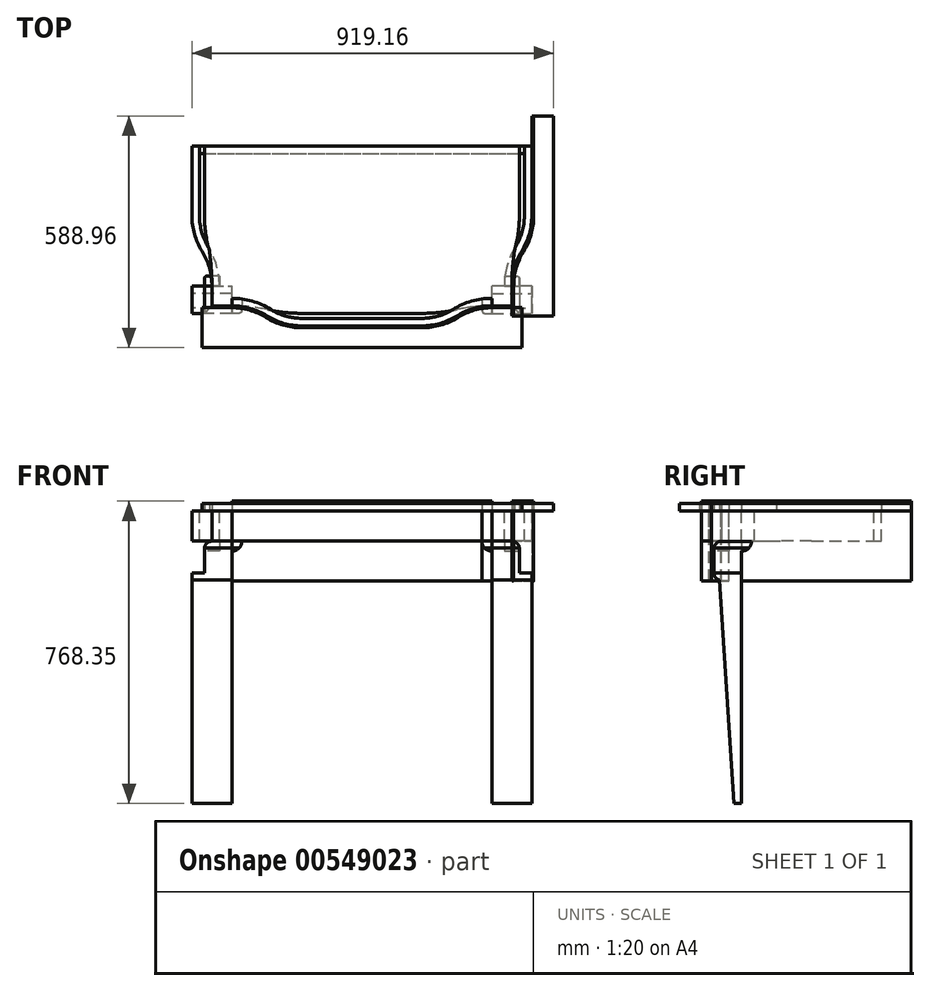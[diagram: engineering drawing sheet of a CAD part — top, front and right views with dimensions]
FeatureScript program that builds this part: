
annotation { "Feature Type Name" : "Feature", "Feature Type Description" : "" }
export const myFeature = defineFeature(function(context is Context, id is Id, definition is map)
    precondition{}
    {
        {
            var Q0;
            Q0=qCreatedBy(makeId("Top.planeOp"),FACE);
            var sketch = newSketch(context, id + "F0", { "sketchPlane" : qUnion([Q0])});
            skLineSegment(sketch, "E0.bottom", {"start": v(381, -203.2) * mm, "end": v(-381, -203.2) * mm});
            skLineSegment(sketch, "E0.top", {"start": v(381, 203.2) * mm, "end": v(-381, 203.2) * mm});
            skLineSegment(sketch, "E0.left", {"start": v(381, -203.2) * mm, "end": v(381, 203.2) * mm});
            skLineSegment(sketch, "E0.right", {"start": v(-381, -203.2) * mm, "end": v(-381, 203.2) * mm});
            skPoint(sketch, "E0.middle", {"position": v(0, 0) * mm});
            skSolve(sketch);
        }
        {
            var Q0;
            Q0=makeQuery(id+"F0.imprint","IMPRINT",FACE,{"disambiguationData":[TD([[makeQuery(id+"F0.imprint","IMPRINT",EDGE,{"derivedFrom":sQuery(id+"F0.wireOp",EDGE,"E0.bottom")}),-1.0]])]});
            var sketch = newSketch(context, id + "F1", { "sketchPlane" : qUnion([Q0])});
            skLineSegment(sketch, "E1.0", {"start": v(-330.2, -203.2) * mm, "end": v(-381, -203.2) * mm});
            skLineSegment(sketch, "E2.right", {"start": v(330.2, -203.2) * mm, "end": v(330.2, -184.15) * mm});
            skLineSegment(sketch, "E3", {"start": v(0, -254) * mm, "end": v(0, 0) * mm, "construction": true});
            skArc(sketch, "E4", {"start": v(-330.2, -203.2) * mm, "mid": v(-283.97, -209.67) * mm, "end": v(-241.3, -228.6) * mm});
            skArc(sketch, "E5", {"start": v(-241.3, -228.6) * mm, "mid": v(-198.63, -247.53) * mm, "end": v(-152.4, -254) * mm});
            skLineSegment(sketch, "E6", {"start": v(-152.4, -254) * mm, "end": v(0, -254) * mm});
            skArc(sketch, "E7.MirrorCS", {"start": v(330.2, -203.2) * mm, "mid": v(283.97, -209.67) * mm, "end": v(241.3, -228.6) * mm});
            skArc(sketch, "E8.MirrorCS", {"start": v(241.3, -228.6) * mm, "mid": v(198.63, -247.53) * mm, "end": v(152.4, -254) * mm});
            skPoint(sketch, "E9.orphan", {"position": v(-381, -254) * mm});
            skPoint(sketch, "E10.orphan", {"position": v(381, -254) * mm});
            skLineSegment(sketch, "E11.MirrorCS", {"start": v(152.4, -254) * mm, "end": v(0, -254) * mm});
            skArc(sketch, "E12.0", {"start": v(-231.24, -212.43) * mm, "mid": v(-193.4, -229.2) * mm, "end": v(-152.4, -234.95) * mm});
            skArc(sketch, "E12.1", {"start": v(-330.2, -184.15) * mm, "mid": v(-278.74, -191.36) * mm, "end": v(-231.24, -212.43) * mm});
            skArc(sketch, "E13.0", {"start": v(231.24, -212.43) * mm, "mid": v(193.4, -229.2) * mm, "end": v(152.4, -234.95) * mm});
            skArc(sketch, "E13.1", {"start": v(330.2, -184.15) * mm, "mid": v(278.74, -191.36) * mm, "end": v(231.24, -212.43) * mm});
            skPoint(sketch, "E14.0.end.orphan", {"position": v(381, 203.2) * mm});
            skPoint(sketch, "E14.0.start.orphan", {"position": v(381, -203.2) * mm});
            skPoint(sketch, "E15.0.end.orphan", {"position": v(-381, 203.2) * mm});
            skPoint(sketch, "E15.0.start.orphan", {"position": v(-381, -203.2) * mm});
            skLineSegment(sketch, "E16", {"start": v(-152.4, -234.95) * mm, "end": v(152.4, -234.95) * mm});
            skLineSegment(sketch, "E17", {"start": v(-330.2, -184.15) * mm, "end": v(-330.2, -203.2) * mm});
            skSolve(sketch);
        }
        {
            var Q0;
            Q0=makeQuery(id+"F0.imprint","IMPRINT",FACE,{"disambiguationData":[TD([[makeQuery(id+"F0.imprint","IMPRINT",EDGE,{"derivedFrom":sQuery(id+"F0.wireOp",EDGE,"E0.bottom")}),-1.0]])]});
            var sketch = newSketch(context, id + "F2", { "sketchPlane" : qUnion([Q0])});
            skLineSegment(sketch, "E18.0", {"start": v(381, -203.2) * mm, "end": v(-381, -203.2) * mm, "construction": true});
            skLineSegment(sketch, "E19.0", {"start": v(-381, -203.2) * mm, "end": v(-381, 203.2) * mm, "construction": true});
            skLineSegment(sketch, "E20.0", {"start": v(381, -203.2) * mm, "end": v(381, 203.2) * mm, "construction": true});
            skLineSegment(sketch, "E21.bottom", {"start": v(431.8, -254) * mm, "end": v(330.2, -254) * mm});
            skLineSegment(sketch, "E21.top", {"start": v(431.8, -152.4) * mm, "end": v(330.2, -152.4) * mm});
            skLineSegment(sketch, "E21.left", {"start": v(431.8, -254) * mm, "end": v(431.8, -152.4) * mm});
            skLineSegment(sketch, "E21.right", {"start": v(330.2, -254) * mm, "end": v(330.2, -152.4) * mm});
            skPoint(sketch, "E21.middle", {"position": v(381, -203.2) * mm});
            skPoint(sketch, "E22.middle", {"position": v(-381, -203.2) * mm});
            skSolve(sketch);
        }
        {
            var Q0;
            Q0=makeQuery(id+"F0.imprint","IMPRINT",FACE,{"disambiguationData":[TD([[makeQuery(id+"F0.imprint","IMPRINT",EDGE,{"derivedFrom":sQuery(id+"F0.wireOp",EDGE,"E0.bottom")}),-1.0]])]});
            var sketch = newSketch(context, id + "F3", { "sketchPlane" : qUnion([Q0])});
            skLineSegment(sketch, "E23.0", {"start": v(-381, -203.2) * mm, "end": v(-381, 203.2) * mm, "construction": true});
            skLineSegment(sketch, "E24.0", {"start": v(-361.95, -152.4) * mm, "end": v(-381, -152.4) * mm});
            skArc(sketch, "E25", {"start": v(-381, -152.4) * mm, "mid": v(-387.47, -106.17) * mm, "end": v(-406.4, -63.5) * mm});
            skArc(sketch, "E26", {"start": v(-431.8, 25.4) * mm, "mid": v(-425.33, -20.83) * mm, "end": v(-406.4, -63.5) * mm});
            skLineSegment(sketch, "E27", {"start": v(-431.8, 25.4) * mm, "end": v(-431.8, 203.2) * mm});
            skArc(sketch, "E28.0", {"start": v(-412.75, 25.4) * mm, "mid": v(-407, -15.6) * mm, "end": v(-390.23, -53.44) * mm});
            skArc(sketch, "E28.1", {"start": v(-361.95, -152.4) * mm, "mid": v(-369.16, -100.94) * mm, "end": v(-390.23, -53.44) * mm});
            skLineSegment(sketch, "E29", {"start": v(-412.75, 25.4) * mm, "end": v(-412.75, 203.2) * mm});
            skLineSegment(sketch, "E30", {"start": v(-412.75, 203.2) * mm, "end": v(-431.8, 203.2) * mm});
            skPoint(sketch, "E31.orphan", {"position": v(-330.2, -152.4) * mm});
            skSolve(sketch);
        }
        {
            var Q0;
            Q0 = qSketchRegion(id + "F3", true);
            extrude(context, id + "F4", {"entities" : qUnion([Q0]), "oppositeDirection" : true, "depth" : 76.2 * mm, "offsetDistance" : 25.4 * mm});
        }
        {
            var Q0;
            Q0 = qSketchRegion(id + "F1", true);
            extrude(context, id + "F5", {"entities" : qUnion([Q0]), "oppositeDirection" : true, "depth" : 76.2 * mm, "offsetDistance" : 25.4 * mm});
        }
        {
            var Q0;
            Q0=makeQuery(id+"F4.opExtrude","SWEPT_BODY",BODY,{"disambiguationData":[OSD([sQuery(id+"F3.wireOp",EDGE,"E24.0"),sQuery(id+"F3.wireOp",EDGE,"E25"),sQuery(id+"F3.wireOp",EDGE,"E26"),sQuery(id+"F3.wireOp",EDGE,"E27"),sQuery(id+"F3.wireOp",EDGE,"E28.0"),sQuery(id+"F3.wireOp",EDGE,"E28.1"),sQuery(id+"F3.wireOp",EDGE,"E29"),sQuery(id+"F3.wireOp",EDGE,"E30")])]});
            var Q1;
            Q1=qCreatedBy(makeId("Right.planeOp"),FACE);
            mirror(context, id + "F6", {"entities" : qUnion([Q0]), "mirrorPlane" : qUnion([Q1])});
        }
        {
            var Q0;
            Q0=makeQuery(id+"F0.imprint","IMPRINT",FACE,{"disambiguationData":[TD([[makeQuery(id+"F0.imprint","IMPRINT",EDGE,{"derivedFrom":sQuery(id+"F0.wireOp",EDGE,"E0.bottom")}),-1.0]])]});
            var sketch = newSketch(context, id + "F7", { "sketchPlane" : qUnion([Q0])});
            skLineSegment(sketch, "E32.0", {"start": v(-381, -203.2) * mm, "end": v(-381, 203.2) * mm, "construction": true});
            skArc(sketch, "E33", {"start": v(-381, -152.4) * mm, "mid": v(-382.59, -107.84) * mm, "end": v(-387.35, -63.5) * mm});
            skLineSegment(sketch, "E34.0", {"start": v(-400.05, 25.4) * mm, "end": v(-400.05, 203.2) * mm});
            skArc(sketch, "E35", {"start": v(-400.05, 25.4) * mm, "mid": v(-396.86, -19.5) * mm, "end": v(-387.35, -63.5) * mm});
            skLineSegment(sketch, "E36", {"start": v(-381, -152.4) * mm, "end": v(-381, -203.2) * mm});
            skPoint(sketch, "E37.0.start.orphan", {"position": v(-330.2, -152.4) * mm});
            skLineSegment(sketch, "E38.0", {"start": v(-152.4, -222.25) * mm, "end": v(152.4, -222.25) * mm});
            skPoint(sketch, "E39.0.end.orphan", {"position": v(-381, -203.2) * mm});
            skPoint(sketch, "E39.0.start.orphan", {"position": v(381, -203.2) * mm});
            skLineSegment(sketch, "E40.0", {"start": v(-330.2, -203.2) * mm, "end": v(-330.2, -152.4) * mm, "construction": true});
            skArc(sketch, "E41", {"start": v(-241.3, -212.73) * mm, "mid": v(-285.5, -205.59) * mm, "end": v(-330.2, -203.2) * mm});
            skArc(sketch, "E42", {"start": v(-241.3, -212.73) * mm, "mid": v(-197.1, -219.86) * mm, "end": v(-152.4, -222.25) * mm});
            skLineSegment(sketch, "E43", {"start": v(-381, -203.2) * mm, "end": v(-330.2, -203.2) * mm});
            skArc(sketch, "E44.MirrorCS", {"start": v(241.3, -212.73) * mm, "mid": v(197.1, -219.86) * mm, "end": v(152.4, -222.25) * mm});
            skArc(sketch, "E45.MirrorCS", {"start": v(241.3, -212.73) * mm, "mid": v(285.5, -205.59) * mm, "end": v(330.2, -203.2) * mm});
            skArc(sketch, "E46.MirrorCS", {"start": v(381, -152.4) * mm, "mid": v(382.59, -107.84) * mm, "end": v(387.35, -63.5) * mm});
            skArc(sketch, "E47.MirrorCS", {"start": v(400.05, 25.4) * mm, "mid": v(396.86, -19.5) * mm, "end": v(387.35, -63.5) * mm});
            skLineSegment(sketch, "E48.MirrorCS", {"start": v(400.05, 25.4) * mm, "end": v(400.05, 203.2) * mm});
            skLineSegment(sketch, "E49.MirrorCS", {"start": v(381, -203.2) * mm, "end": v(330.2, -203.2) * mm});
            skLineSegment(sketch, "E50", {"start": v(381, -152.4) * mm, "end": v(381, -203.2) * mm});
            skLineSegment(sketch, "E51", {"start": v(-400.05, 203.2) * mm, "end": v(400.05, 203.2) * mm});
            skSolve(sketch);
        }
        {
            var Q0;
            Q0 = qSketchRegion(id + "F7", true);
            extrude(context, id + "F8", {"entities" : qUnion([Q0]), "depth" : 19.05 * mm, "offsetDistance" : 25.4 * mm});
        }
        {
            var Q0;
            Q0 = qSketchRegion(id + "F2", true);
            extrude(context, id + "F9", {"entities" : qUnion([Q0]), "oppositeDirection" : true, "depth" : 742.95 * mm, "offsetDistance" : 25.4 * mm});
        }
        {
            var Q0;
            Q0=makeQuery(id+"F9.opExtrude","SWEPT_FACE",FACE,{"disambiguationData":[OSD([sQuery(id+"F2.wireOp",EDGE,"E21.left")])]});
            var sketch = newSketch(context, id + "F10", { "sketchPlane" : qUnion([Q0])});
            skLineSegment(sketch, "E52", {"start": v(-203.2, -76.2) * mm, "end": v(-152.4, -76.2) * mm, "construction": true});
            skLineSegment(sketch, "E53", {"start": v(-203.2, 0) * mm, "end": v(-203.2, -76.2) * mm});
            skArc(sketch, "E54", {"start": v(-203.2, -76.2) * mm, "mid": v(-216.03, -81.17) * mm, "end": v(-222.17, -93.49) * mm});
            skLineSegment(sketch, "E55", {"start": v(-222.17, -93.49) * mm, "end": v(-222.17, -156.99) * mm});
            skPoint(sketch, "E56.end.orphan", {"position": v(-171.45, -742.95) * mm});
            skArc(sketch, "E57", {"start": v(-222.17, -156.99) * mm, "mid": v(-218.46, -168.28) * mm, "end": v(-208.78, -175.18) * mm});
            skLineSegment(sketch, "E58", {"start": v(-208.78, -175.18) * mm, "end": v(-171.45, -742.95) * mm});
            skSolve(sketch);
        }
        {
            var Q0;
            {var subQ0=sQuery(id+"F10.wireOp",EDGE,"E53");Q0=makeQuery(id+"F10.imprint","IMPRINT",FACE,{"disambiguationData":[TD([[makeQuery(id+"F10.imprint","IMPRINT",EDGE,{"derivedFrom":subQ0}),-1.0]])]});}
            extrude(context, id + "F11", {"entities" : qUnion([Q0]), "operationType" : NewBodyOperationType.REMOVE, "oppositeDirection" : true, "depth" : 127 * mm, "offsetDistance" : 25.4 * mm});
        }
        {
            var Q0;
            Q0=makeQuery(id+"F11.boolean.opBoolean","COPY",FACE,{"derivedFrom":makeQuery(id+"F11.opExtrude","SWEPT_FACE",FACE,{"disambiguationData":[OSD([sQuery(id+"F10.wireOp",EDGE,"E55")])]})});
            var sketch = newSketch(context, id + "F12", { "sketchPlane" : qUnion([Q0])});
            skLineSegment(sketch, "E59.0", {"start": v(381, 0) * mm, "end": v(431.8, 0) * mm});
            skLineSegment(sketch, "E60.0", {"start": v(431.8, 0) * mm, "end": v(431.8, -76.2) * mm});
            skLineSegment(sketch, "E61", {"start": v(381, 0) * mm, "end": v(381, -76.2) * mm});
            skArc(sketch, "E62", {"start": v(399.97, -93.55) * mm, "mid": v(393.85, -81.19) * mm, "end": v(381, -76.2) * mm});
            skLineSegment(sketch, "E63", {"start": v(399.97, -93.55) * mm, "end": v(399.97, -156.99) * mm});
            skArc(sketch, "E64", {"start": v(399.97, -156.99) * mm, "mid": v(396.42, -168.07) * mm, "end": v(387.08, -175.02) * mm});
            skLineSegment(sketch, "E65", {"start": v(387.08, -175.02) * mm, "end": v(349.25, -742.95) * mm});
            skPoint(sketch, "E66.0", {"position": v(381, -742.95) * mm});
            skLineSegment(sketch, "E67.0", {"start": v(349.25, -742.95) * mm, "end": v(431.8, -742.95) * mm});
            skLineSegment(sketch, "E68.0", {"start": v(431.8, -175.18) * mm, "end": v(431.8, -742.95) * mm});
            skPoint(sketch, "E69.orphan", {"position": v(330.2, -742.95) * mm});
            skLineSegment(sketch, "E70.0", {"start": v(431.8, -156.99) * mm, "end": v(431.8, -175.18) * mm});
            skLineSegment(sketch, "E71.0", {"start": v(431.8, -93.49) * mm, "end": v(431.8, -156.99) * mm});
            skPoint(sketch, "E72.0", {"position": v(431.8, -81.17) * mm});
            skLineSegment(sketch, "E73.0", {"start": v(431.8, -76.2) * mm, "end": v(431.8, -93.49) * mm});
            skPoint(sketch, "E74.orphan", {"position": v(330.2, 0) * mm});
            skSolve(sketch);
        }
        {
            var Q0;
            {var subQ0=sQuery(id+"F12.wireOp",EDGE,"E64");Q0=makeQuery(id+"F12.imprint","IMPRINT",FACE,{"disambiguationData":[TD([[makeQuery(id+"F12.imprint","IMPRINT",EDGE,{"derivedFrom":subQ0}),1.0]])]});}
            var Q1;
            {var subQ5=sQuery(id+"F12.wireOp",EDGE,"E63");Q1=makeQuery(id+"F12.imprint","IMPRINT",FACE,{"disambiguationData":[TD([[makeQuery(id+"F12.imprint","IMPRINT",EDGE,{"derivedFrom":subQ5}),1.0]])]});}
            var Q2;
            Q2=makeQuery(id+"F12.imprint","IMPRINT",FACE,{"disambiguationData":[TD([[makeQuery(id+"F12.imprint","IMPRINT",EDGE,{"derivedFrom":sQuery(id+"F12.wireOp",EDGE,"E59.0")}),-1.0]])]});
            extrude(context, id + "F13", {"entities" : qUnion([Q0, Q1, Q2]), "operationType" : NewBodyOperationType.REMOVE, "oppositeDirection" : true, "depth" : 101.6 * mm, "offsetDistance" : 25.4 * mm});
        }
        {
            var Q0;
            Q0=makeQuery(id+"F9.opExtrude","SWEPT_BODY",BODY,{"disambiguationData":[OSD([sQuery(id+"F2.wireOp",EDGE,"E21.bottom"),sQuery(id+"F2.wireOp",EDGE,"E21.top"),sQuery(id+"F2.wireOp",EDGE,"E21.left"),sQuery(id+"F2.wireOp",EDGE,"E21.right")])]});
            var Q1;
            Q1=qCreatedBy(makeId("Right.planeOp"),FACE);
            mirror(context, id + "F14", {"entities" : qUnion([Q0]), "mirrorPlane" : qUnion([Q1])});
        }
        {
            var Q0;
            Q0=makeQuery(id+"F9.opExtrude","SWEPT_FACE",FACE,{"disambiguationData":[OSD([sQuery(id+"F2.wireOp",EDGE,"E21.right")])]});
            var sketch = newSketch(context, id + "F15", { "sketchPlane" : qUnion([Q0])});
            skLineSegment(sketch, "E75.0", {"start": v(152.4, -742.95) * mm, "end": v(152.4, 0) * mm, "construction": true});
            skLineSegment(sketch, "E76.0.0", {"start": v(171.45, -742.95) * mm, "end": v(208.78, -175.18) * mm, "construction": true});
            skArc(sketch, "E76.0.1", {"start": v(208.78, -175.18) * mm, "mid": v(218.46, -168.28) * mm, "end": v(222.17, -156.99) * mm, "construction": true});
            skLineSegment(sketch, "E76.0.2", {"start": v(222.17, -156.99) * mm, "end": v(222.17, -93.49) * mm, "construction": true});
            skArc(sketch, "E76.0.3", {"start": v(222.17, -93.49) * mm, "mid": v(216.03, -81.17) * mm, "end": v(203.2, -76.2) * mm});
            skLineSegment(sketch, "E76.0.4", {"start": v(203.2, -76.2) * mm, "end": v(203.2, 0) * mm});
            skLineSegment(sketch, "E76.0.5", {"start": v(203.2, 0) * mm, "end": v(152.4, 0) * mm, "construction": true});
            skLineSegment(sketch, "E76.0.6", {"start": v(152.4, 0) * mm, "end": v(152.4, -742.95) * mm});
            skLineSegment(sketch, "E76.0.7", {"start": v(152.4, -742.95) * mm, "end": v(171.45, -742.95) * mm, "construction": true});
            skLineSegment(sketch, "E77.0", {"start": v(184.15, -76.2) * mm, "end": v(184.15, 0) * mm, "construction": true});
            skLineSegment(sketch, "E78.0", {"start": v(184.15, -76.2) * mm, "end": v(203.2, -76.2) * mm});
            skLineSegment(sketch, "E79", {"start": v(184.15, -76.2) * mm, "end": v(184.15, -101.6) * mm});
            skLineSegment(sketch, "E80", {"start": v(184.15, -101.6) * mm, "end": v(222.17, -101.6) * mm});
            skSolve(sketch);
        }
        {
            var Q0;
            {var subQ1=sQuery(id+"F15.wireOp",EDGE,"E76.0.3");Q0=makeQuery(id+"F15.imprint","IMPRINT",FACE,{"disambiguationData":[TD([[makeQuery(id+"F15.imprint","IMPRINT",EDGE,{"derivedFrom":subQ1}),-1.0]])]});}
            extrude(context, id + "F16", {"entities" : qUnion([Q0]), "depth" : 25.4 * mm, "offsetDistance" : 25.4 * mm});
        }
        {
            var Q0;
            Q0=makeQuery(id+"F16.opExtrude","SWEPT_FACE",FACE,{"disambiguationData":[OSD([sQuery(id+"F2.wireOp",EDGE,"E21.right"),sQuery(id+"F10.wireOp",EDGE,"E55")])]});
            var sketch = newSketch(context, id + "F17", { "sketchPlane" : qUnion([Q0])});
            skLineSegment(sketch, "E81.0", {"start": v(304.8, -76.2) * mm, "end": v(304.8, -93.49) * mm});
            skLineSegment(sketch, "E82.0", {"start": v(304.8, -93.49) * mm, "end": v(304.8, -101.6) * mm});
            skLineSegment(sketch, "E83.0", {"start": v(304.8, -101.6) * mm, "end": v(330.2, -101.6) * mm});
            skArc(sketch, "E84", {"start": v(304.8, -76.2) * mm, "mid": v(312.24, -94.16) * mm, "end": v(330.2, -101.6) * mm});
            skSolve(sketch);
        }
        {
            var Q0;
            {var subQ0=sQuery(id+"F17.wireOp",EDGE,"E81.0");Q0=makeQuery(id+"F17.imprint","IMPRINT",FACE,{"disambiguationData":[TD([[makeQuery(id+"F17.imprint","IMPRINT",EDGE,{"derivedFrom":subQ0}),1.0]])]});}
            var Q1;
            {var subQ0=sQuery(id+"F17.wireOp",EDGE,"E82.0");Q1=makeQuery(id+"F17.imprint","IMPRINT",FACE,{"disambiguationData":[TD([[makeQuery(id+"F17.imprint","IMPRINT",EDGE,{"derivedFrom":subQ0}),1.0]])]});}
            extrude(context, id + "F18", {"entities" : qUnion([Q0, Q1]), "operationType" : NewBodyOperationType.REMOVE, "oppositeDirection" : true, "depth" : 50.8 * mm, "offsetDistance" : 25.4 * mm});
        }
        {
            var Q0;
            Q0=makeQuery(id+"F9.opExtrude","SWEPT_FACE",FACE,{"disambiguationData":[OSD([sQuery(id+"F2.wireOp",EDGE,"E21.top")])]});
            var sketch = newSketch(context, id + "F19", { "sketchPlane" : qUnion([Q0])});
            skArc(sketch, "E85.0", {"start": v(-381, -76.2) * mm, "mid": v(-393.85, -81.19) * mm, "end": v(-399.97, -93.55) * mm});
            skLineSegment(sketch, "E86.0", {"start": v(-399.97, -101.6) * mm, "end": v(-399.97, -93.55) * mm});
            skLineSegment(sketch, "E87.0", {"start": v(-361.95, -76.2) * mm, "end": v(-381, -76.2) * mm});
            skLineSegment(sketch, "E88", {"start": v(-361.95, -76.2) * mm, "end": v(-361.95, -101.6) * mm});
            skLineSegment(sketch, "E89", {"start": v(-361.95, -101.6) * mm, "end": v(-399.97, -101.6) * mm});
            skPoint(sketch, "E90.orphan", {"position": v(-399.97, -156.99) * mm});
            skSolve(sketch);
        }
        {
            var Q0;
            Q0=makeQuery(id+"F19.imprint","IMPRINT",FACE,{"disambiguationData":[TD([[makeQuery(id+"F19.imprint","IMPRINT",EDGE,{"derivedFrom":sQuery(id+"F19.wireOp",EDGE,"E85.0")}),1.0]])]});
            extrude(context, id + "F20", {"entities" : qUnion([Q0]), "depth" : 25.4 * mm, "offsetDistance" : 25.4 * mm});
        }
        {
            var Q0;
            Q0=makeQuery(id+"F20.opExtrude","SWEPT_FACE",FACE,{"disambiguationData":[OSD([sQuery(id+"F19.wireOp",EDGE,"E86.0")])]});
            var sketch = newSketch(context, id + "F21", { "sketchPlane" : qUnion([Q0])});
            skLineSegment(sketch, "E91.0", {"start": v(-127, -76.2) * mm, "end": v(-127, -93.55) * mm});
            skLineSegment(sketch, "E92.0", {"start": v(-127, -101.6) * mm, "end": v(-127, -93.55) * mm});
            skLineSegment(sketch, "E93.0", {"start": v(-127, -101.6) * mm, "end": v(-152.4, -101.6) * mm});
            skArc(sketch, "E94", {"start": v(-152.4, -101.6) * mm, "mid": v(-134.44, -94.16) * mm, "end": v(-127, -76.2) * mm});
            skSolve(sketch);
        }
        {
            var Q0;
            {var subQ0=sQuery(id+"F21.wireOp",EDGE,"E91.0");Q0=makeQuery(id+"F21.imprint","IMPRINT",FACE,{"disambiguationData":[TD([[makeQuery(id+"F21.imprint","IMPRINT",EDGE,{"derivedFrom":subQ0}),-1.0]])]});}
            var Q1;
            {var subQ0=sQuery(id+"F21.wireOp",EDGE,"E92.0");Q1=makeQuery(id+"F21.imprint","IMPRINT",FACE,{"disambiguationData":[TD([[makeQuery(id+"F21.imprint","IMPRINT",EDGE,{"derivedFrom":subQ0}),1.0]])]});}
            extrude(context, id + "F22", {"entities" : qUnion([Q0, Q1]), "operationType" : NewBodyOperationType.REMOVE, "oppositeDirection" : true, "depth" : 50.8 * mm, "offsetDistance" : 25.4 * mm});
        }
        {
            var Q0;
            Q0=makeQuery(id+"F16.opExtrude","SWEPT_BODY",BODY,{"disambiguationData":[OSD([sQuery(id+"F2.wireOp",EDGE,"E21.right"),sQuery(id+"F10.wireOp",EDGE,"E55"),sQuery(id+"F15.wireOp",EDGE,"E76.0.3"),sQuery(id+"F15.wireOp",EDGE,"E78.0"),sQuery(id+"F15.wireOp",EDGE,"E79"),sQuery(id+"F15.wireOp",EDGE,"E80")])]});
            var Q1;
            Q1=makeQuery(id+"F20.opExtrude","SWEPT_BODY",BODY,{"disambiguationData":[OSD([sQuery(id+"F19.wireOp",EDGE,"E85.0"),sQuery(id+"F19.wireOp",EDGE,"E86.0"),sQuery(id+"F19.wireOp",EDGE,"E87.0"),sQuery(id+"F19.wireOp",EDGE,"E88"),sQuery(id+"F19.wireOp",EDGE,"E89")])]});
            var Q2;
            Q2=qCreatedBy(makeId("Right.planeOp"),FACE);
            mirror(context, id + "F23", {"entities" : qUnion([Q0, Q1]), "mirrorPlane" : qUnion([Q2])});
        }
        {
            var Q0;
            Q0=makeQuery(id+"F0.imprint","IMPRINT",FACE,{"disambiguationData":[TD([[makeQuery(id+"F0.imprint","IMPRINT",EDGE,{"derivedFrom":sQuery(id+"F0.wireOp",EDGE,"E0.bottom")}),-1.0]])]});
            var sketch = newSketch(context, id + "F24", { "sketchPlane" : qUnion([Q0])});
            skLineSegment(sketch, "E95.0", {"start": v(-412.75, 184.15) * mm, "end": v(-412.75, 203.2) * mm});
            skLineSegment(sketch, "E96.0", {"start": v(412.75, 184.15) * mm, "end": v(412.75, 203.2) * mm});
            skLineSegment(sketch, "E97", {"start": v(-412.75, 203.2) * mm, "end": v(412.75, 203.2) * mm});
            skLineSegment(sketch, "E98.0", {"start": v(-412.75, 184.15) * mm, "end": v(412.75, 184.15) * mm});
            skPoint(sketch, "E99.orphan", {"position": v(-412.75, 25.4) * mm});
            skPoint(sketch, "E100.orphan", {"position": v(412.75, 25.4) * mm});
            skSolve(sketch);
        }
        {
            var Q0;
            Q0 = qSketchRegion(id + "F24", true);
            extrude(context, id + "F25", {"entities" : qUnion([Q0]), "oppositeDirection" : true, "depth" : 76.2 * mm, "offsetDistance" : 25.4 * mm});
        }
        {
            var Q0;
            Q0=makeQuery(id+"F6.opPattern","COPY",FACE,{"derivedFrom":makeQuery(id+"F4.opExtrude","CAP_FACE",FACE,{"disambiguationData":[OSD([sQuery(id+"F3.wireOp",EDGE,"E24.0"),sQuery(id+"F3.wireOp",EDGE,"E25"),sQuery(id+"F3.wireOp",EDGE,"E26"),sQuery(id+"F3.wireOp",EDGE,"E27"),sQuery(id+"F3.wireOp",EDGE,"E28.0"),sQuery(id+"F3.wireOp",EDGE,"E28.1"),sQuery(id+"F3.wireOp",EDGE,"E29"),sQuery(id+"F3.wireOp",EDGE,"E30")])],"isStart":true}),"instanceName":"1"});
            var sketch = newSketch(context, id + "F26", { "sketchPlane" : qUnion([Q0])});
            skLineSegment(sketch, "E101.0", {"start": v(431.8, 25.4) * mm, "end": v(431.8, 203.2) * mm});
            skArc(sketch, "E102.0", {"start": v(431.8, 25.4) * mm, "mid": v(425.33, -20.83) * mm, "end": v(406.4, -63.5) * mm});
            skArc(sketch, "E103.0", {"start": v(381, -152.4) * mm, "mid": v(387.47, -106.17) * mm, "end": v(406.4, -63.5) * mm});
            skLineSegment(sketch, "E104", {"start": v(431.8, 203.2) * mm, "end": v(431.8, 279.4) * mm});
            skLineSegment(sketch, "E105", {"start": v(381, -152.4) * mm, "end": v(381, -228.6) * mm});
            skLineSegment(sketch, "E106.0", {"start": v(436.56, 203.2) * mm, "end": v(436.56, 279.4) * mm});
            skLineSegment(sketch, "E106.1", {"start": v(385.76, -152.4) * mm, "end": v(385.76, -228.6) * mm});
            skArc(sketch, "E106.2", {"start": v(385.76, -152.4) * mm, "mid": v(392.05, -107.48) * mm, "end": v(410.44, -66.02) * mm});
            skArc(sketch, "E106.3", {"start": v(436.56, 25.4) * mm, "mid": v(429.9, -22.14) * mm, "end": v(410.44, -66.02) * mm});
            skLineSegment(sketch, "E106.4", {"start": v(436.56, 25.4) * mm, "end": v(436.56, 203.2) * mm});
            skLineSegment(sketch, "E107", {"start": v(436.56, 279.4) * mm, "end": v(487.36, 279.4) * mm});
            skLineSegment(sketch, "E108", {"start": v(487.36, 279.4) * mm, "end": v(487.36, -228.6) * mm});
            skLineSegment(sketch, "E109", {"start": v(487.36, -228.6) * mm, "end": v(385.76, -228.6) * mm});
            skLineSegment(sketch, "E110", {"start": v(381, -228.6) * mm, "end": v(385.76, -228.6) * mm});
            skLineSegment(sketch, "E111", {"start": v(431.8, 279.4) * mm, "end": v(436.56, 279.4) * mm});
            skSolve(sketch);
        }
        {
            var Q0;
            Q0=makeQuery(id+"F26.imprint","IMPRINT",FACE,{"disambiguationData":[TD([[makeQuery(id+"F26.imprint","IMPRINT",EDGE,{"derivedFrom":sQuery(id+"F26.wireOp",EDGE,"E101.0")}),-1.0]])]});
            extrude(context, id + "F27", {"entities" : qUnion([Q0]), "depth" : 25.4 * mm, "offsetDistance" : 25.4 * mm});
        }
        {
            var Q0;
            Q0=makeQuery(id+"F26.imprint","IMPRINT",FACE,{"disambiguationData":[TD([[makeQuery(id+"F26.imprint","IMPRINT",EDGE,{"derivedFrom":sQuery(id+"F26.wireOp",EDGE,"E101.0")}),-1.0]])]});
            extrude(context, id + "F28", {"entities" : qUnion([Q0]), "operationType" : NewBodyOperationType.ADD, "oppositeDirection" : true, "depth" : 177.8 * mm, "offsetDistance" : 25.4 * mm});
        }
        {
            var Q0;
            Q0=makeQuery(id+"F5.opExtrude","CAP_FACE",FACE,{"disambiguationData":[OSD([sQuery(id+"F1.wireOp",EDGE,"E2.right"),sQuery(id+"F1.wireOp",EDGE,"E4"),sQuery(id+"F1.wireOp",EDGE,"E5"),sQuery(id+"F1.wireOp",EDGE,"E6"),sQuery(id+"F1.wireOp",EDGE,"E7.MirrorCS"),sQuery(id+"F1.wireOp",EDGE,"E8.MirrorCS"),sQuery(id+"F1.wireOp",EDGE,"E11.MirrorCS"),sQuery(id+"F1.wireOp",EDGE,"E12.0"),sQuery(id+"F1.wireOp",EDGE,"E12.1"),sQuery(id+"F1.wireOp",EDGE,"E13.0"),sQuery(id+"F1.wireOp",EDGE,"E13.1"),sQuery(id+"F1.wireOp",EDGE,"E16"),sQuery(id+"F1.wireOp",EDGE,"E17")])],"isStart":true});
            var sketch = newSketch(context, id + "F29", { "sketchPlane" : qUnion([Q0])});
            skArc(sketch, "E112.0", {"start": v(-330.2, -203.2) * mm, "mid": v(-283.97, -209.67) * mm, "end": v(-241.3, -228.6) * mm});
            skArc(sketch, "E113.0", {"start": v(-241.3, -228.6) * mm, "mid": v(-198.63, -247.53) * mm, "end": v(-152.4, -254) * mm});
            skLineSegment(sketch, "E114.0", {"start": v(-152.4, -254) * mm, "end": v(152.4, -254) * mm});
            skArc(sketch, "E115.0", {"start": v(241.3, -228.6) * mm, "mid": v(198.63, -247.53) * mm, "end": v(152.4, -254) * mm});
            skArc(sketch, "E116.0", {"start": v(330.2, -203.2) * mm, "mid": v(283.97, -209.67) * mm, "end": v(241.3, -228.6) * mm});
            skLineSegment(sketch, "E117", {"start": v(-330.2, -203.2) * mm, "end": v(-406.4, -203.2) * mm});
            skLineSegment(sketch, "E118", {"start": v(330.2, -203.2) * mm, "end": v(406.4, -203.2) * mm});
            skArc(sketch, "E119.0", {"start": v(330.2, -207.96) * mm, "mid": v(285.28, -214.25) * mm, "end": v(243.82, -232.64) * mm});
            skArc(sketch, "E119.1", {"start": v(-330.2, -207.96) * mm, "mid": v(-285.28, -214.25) * mm, "end": v(-243.82, -232.64) * mm});
            skArc(sketch, "E119.2", {"start": v(-243.82, -232.64) * mm, "mid": v(-199.94, -252.1) * mm, "end": v(-152.4, -258.76) * mm});
            skLineSegment(sketch, "E119.3", {"start": v(-152.4, -258.76) * mm, "end": v(152.4, -258.76) * mm});
            skArc(sketch, "E119.4", {"start": v(243.82, -232.64) * mm, "mid": v(199.94, -252.1) * mm, "end": v(152.4, -258.76) * mm});
            skLineSegment(sketch, "E120", {"start": v(330.2, -207.96) * mm, "end": v(406.4, -207.96) * mm});
            skLineSegment(sketch, "E121", {"start": v(406.4, -207.96) * mm, "end": v(406.4, -309.56) * mm});
            skLineSegment(sketch, "E122", {"start": v(406.4, -203.2) * mm, "end": v(406.4, -207.96) * mm});
            skPoint(sketch, "E123.start.orphan", {"position": v(-330.2, -309.56) * mm});
            skLineSegment(sketch, "E124", {"start": v(406.4, -309.56) * mm, "end": v(-406.4, -309.56) * mm});
            skLineSegment(sketch, "E125", {"start": v(-406.4, -309.56) * mm, "end": v(-406.4, -203.2) * mm});
            skLineSegment(sketch, "E126", {"start": v(-330.2, -207.96) * mm, "end": v(-406.4, -207.96) * mm});
            skSolve(sketch);
        }
        {
            var Q0;
            Q0=makeQuery(id+"F29.imprint","IMPRINT",FACE,{"disambiguationData":[TD([[makeQuery(id+"F29.imprint","IMPRINT",EDGE,{"derivedFrom":sQuery(id+"F29.wireOp",EDGE,"E112.0")}),-1.0]])]});
            extrude(context, id + "F30", {"entities" : qUnion([Q0]), "depth" : 25.4 * mm, "offsetDistance" : 25.4 * mm});
        }
        {
            var Q0;
            Q0=makeQuery(id+"F30.opExtrude","CAP_FACE",FACE,{"disambiguationData":[OSD([sQuery(id+"F29.wireOp",EDGE,"E112.0"),sQuery(id+"F29.wireOp",EDGE,"E113.0"),sQuery(id+"F29.wireOp",EDGE,"E114.0"),sQuery(id+"F29.wireOp",EDGE,"E115.0"),sQuery(id+"F29.wireOp",EDGE,"E116.0"),sQuery(id+"F29.wireOp",EDGE,"E117"),sQuery(id+"F29.wireOp",EDGE,"E118"),sQuery(id+"F29.wireOp",EDGE,"E119.0"),sQuery(id+"F29.wireOp",EDGE,"E119.1"),sQuery(id+"F29.wireOp",EDGE,"E119.2"),sQuery(id+"F29.wireOp",EDGE,"E119.3"),sQuery(id+"F29.wireOp",EDGE,"E119.4"),sQuery(id+"F29.wireOp",EDGE,"E120"),sQuery(id+"F29.wireOp",EDGE,"E122"),sQuery(id+"F29.wireOp",EDGE,"E125"),sQuery(id+"F29.wireOp",EDGE,"E126")])],"isStart":true});
            extrude(context, id + "F31", {"entities" : qUnion([Q0]), "depth" : 177.8 * mm, "offsetDistance" : 25.4 * mm});
        }
        {
            var Q0;
            Q0=makeQuery(id+"F29.imprint","IMPRINT",FACE,{"disambiguationData":[TD([[makeQuery(id+"F29.imprint","IMPRINT",EDGE,{"derivedFrom":sQuery(id+"F29.wireOp",EDGE,"E119.0")}),1.0]])]});
            extrude(context, id + "F32", {"entities" : qUnion([Q0]), "depth" : 19.05 * mm, "offsetDistance" : 25.4 * mm});
        }
        {
            var Q0;
            Q0=makeQuery(id+"F26.imprint","IMPRINT",FACE,{"disambiguationData":[TD([[makeQuery(id+"F26.imprint","IMPRINT",EDGE,{"derivedFrom":sQuery(id+"F26.wireOp",EDGE,"E106.0")}),-1.0]])]});
            extrude(context, id + "F33", {"entities" : qUnion([Q0]), "depth" : 19.05 * mm, "offsetDistance" : 25.4 * mm});
        }
    });
